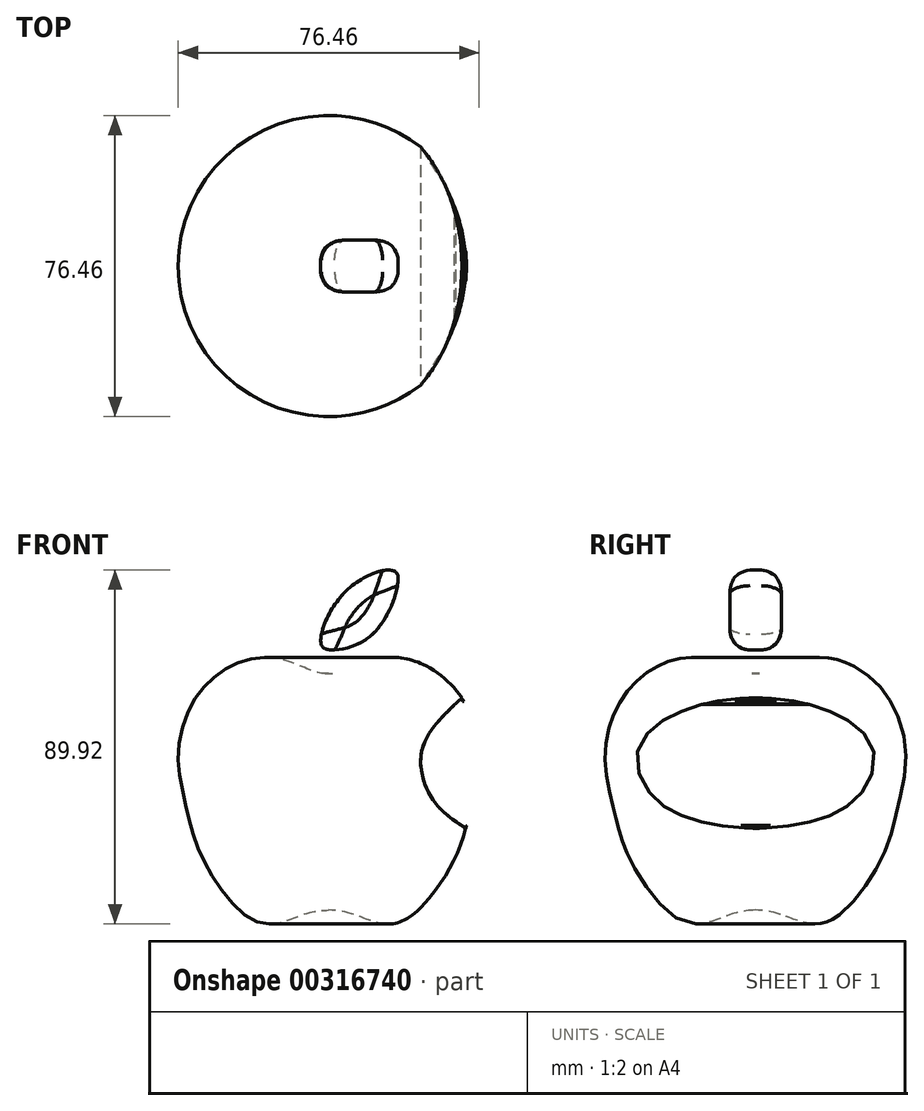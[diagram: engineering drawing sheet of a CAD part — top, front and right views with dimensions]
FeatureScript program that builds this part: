
annotation { "Feature Type Name" : "Feature", "Feature Type Description" : "" }
export const myFeature = defineFeature(function(context is Context, id is Id, definition is map)
    precondition{}
    {
        {
            var Q0;
            Q0=qCreatedBy(makeId("Front.planeOp"),FACE);
            var sketch = newSketch(context, id + "F0", { "sketchPlane" : qUnion([Q0])});
            skFitSpline(sketch, "E0", {"points": [v(0, 11.36) * mm, v(-2.96, 11.6) * mm, v(-11, 14.68) * mm, v(-20.48, 14.91) * mm, v(-28.76, 10.65) * mm, v(-35.15, 2.84) * mm, v(-38.23, -9.47) * mm, v(-36.57, -20.83) * mm, v(-33.73, -31.48) * mm, v(-28.29, -42.14) * mm, v(-19.06, -51.37) * mm, v(-11.95, -51.84) * mm, v(-5.09, -49.47) * mm, v(0, -48.76) * mm], "startDerivative": vector(-59.65, -3.1) * mm, "endDerivative": vector(84.75, 5.4) * mm});
            skLineSegment(sketch, "E1", {"start": v(0, 11.36) * mm, "end": v(0, -48.76) * mm});
            skLineSegment(sketch, "E2", {"start": v(0, 47.58) * mm, "end": v(0, -62.73) * mm, "construction": true});
            skSolve(sketch);
        }
        {
            var Q0;
            Q0=makeQuery(id+"F0.imprint","IMPRINT",FACE,{"disambiguationData":[TD([[makeQuery(id+"F0.imprint","IMPRINT",EDGE,{"derivedFrom":sQuery(id+"F0.wireOp",EDGE,"E0")}),1.0]])]});
            var Q1;
            Q1=sQuery(id+"F0.wireOp",EDGE,"E2");
            revolve(context, id + "F1", {"entities" : qUnion([Q0]), "axis" : qUnion([Q1]), "revolveType" : RevolveType.FULL});
        }
        {
            var Q0;
            Q0=qCreatedBy(makeId("Front.planeOp"),FACE);
            var sketch = newSketch(context, id + "F2", { "sketchPlane" : qUnion([Q0])});
            skFitSpline(sketch, "E3", {"points": [v(16.6, 37.42) * mm, v(4.82, 32.7) * mm, v(-2, 19.3) * mm, v(0, 17.41) * mm, v(10.7, 20.94) * mm, v(17.53, 33.89) * mm, v(16.6, 37.42) * mm]});
            skFitSpline(sketch, "E4", {"points": [v(34.54, 6.49) * mm, v(24.6, -3.3) * mm, v(23.65, -13.65) * mm, v(28.12, -23.06) * mm, v(35.18, -28.8) * mm, v(34.46, -29.02) * mm], "startDerivative": vector(-39.13, -36.51) * mm, "endDerivative": vector(-2.65, 8.88) * mm});
            skFitSpline(sketch, "E5", {"points": [v(34.52, -29.2) * mm, v(38.93, -14.77) * mm, v(34.52, 6.59) * mm, v(34.54, 6.49) * mm], "startDerivative": vector(14.06, 34.1) * mm, "endDerivative": vector(-15.1, 5.38) * mm});
            skLineSegment(sketch, "E6", {"start": v(34.54, 6.49) * mm, "end": v(34.52, -29.2) * mm, "construction": true});
            skLineSegment(sketch, "E7", {"start": v(34.73, 6.42) * mm, "end": v(34.71, -11.36) * mm});
            skPoint(sketch, "E7.endSnap0", {"position": v(34.53, -11.36) * mm});
            skSolve(sketch);
        }
        {
            var Q0;
            Q0=makeQuery(id+"F2.imprint","IMPRINT",FACE,{"disambiguationData":[TD([[makeQuery(id+"F2.imprint","IMPRINT",EDGE,{"derivedFrom":sQuery(id+"F2.wireOp",EDGE,"E3")}),1.0]])]});
            extrude(context, id + "F3", {"entities" : qUnion([Q0]), "endBound" : BoundingType.SYMMETRIC, "depth" : 13.13 * mm});
        }
        {
            var Q0;
            Q0=makeQuery(id+"F3.opExtrude","CAP_FACE",FACE,{"disambiguationData":[OSD([sQuery(id+"F2.wireOp",EDGE,"E3")])],"isStart":false});
            var Q1;
            Q1=makeQuery(id+"F3.opExtrude","CAP_EDGE",EDGE,{"disambiguationData":[OSD([sQuery(id+"F2.wireOp",EDGE,"E3")])],"isStart":true});
            fillet(context, id + "F4", {"entities" : qUnion([Q0, Q1]), "radius" : 5.08 * mm, "tangentPropagation" : true, "allowEdgeOverflow" : false});
        }
        {
            var Q0;
            Q0=qCreatedBy(makeId("Right.planeOp"),FACE);
            cPlane(context, id + "F5", {"entities" : qUnion([Q0]), "cplaneType" : CPlaneType.OFFSET, "offset" : 39.62 * mm, "width" : 152.4 * mm, "height" : 152.4 * mm});
        }
        {
            var Q0;
            Q0=qCreatedBy(makeId("Right.planeOp"),FACE);
            cPlane(context, id + "F6", {"entities" : qUnion([Q0]), "cplaneType" : CPlaneType.OFFSET, "offset" : 23.1 * mm, "width" : 152.4 * mm, "height" : 152.4 * mm});
        }
        {
            var Q0;
            Q0=qCreatedBy(makeId("Right.planeOp"),FACE);
            cPlane(context, id + "F7", {"entities" : qUnion([Q0]), "cplaneType" : CPlaneType.OFFSET, "offset" : 30.48 * mm, "width" : 152.4 * mm, "height" : 152.4 * mm});
        }
        {
            var Q0;
            Q0=qCreatedBy(makeId("Front.planeOp"),FACE);
            var sketch = newSketch(context, id + "F8", { "sketchPlane" : qUnion([Q0])});
            skFitSpline(sketch, "E8", {"points": [v(33.94, 5.23) * mm, v(25.86, -3.37) * mm, v(23.37, -11.03) * mm, v(26.67, -21.01) * mm, v(34.83, -28) * mm], "startDerivative": vector(-34.13, -31.9) * mm, "endDerivative": vector(35.43, -23.64) * mm});
            skLineSegment(sketch, "E9", {"start": v(34.83, -28) * mm, "end": v(33.94, 5.23) * mm});
            skSolve(sketch);
        }
        {
            var Q0;
            Q0=makeQuery(id+"F8.imprint","IMPRINT",FACE,{"disambiguationData":[TD([[makeQuery(id+"F8.imprint","IMPRINT",EDGE,{"derivedFrom":sQuery(id+"F8.wireOp",EDGE,"E8")}),1.0]])]});
            extrude(context, id + "F9", {"entities" : qUnion([Q0]), "operationType" : NewBodyOperationType.REMOVE, "endBound" : BoundingType.SYMMETRIC, "depth" : 101.6 * mm});
        }
        {
            var Q0;
            Q0=qCreatedBy(makeId("Front.planeOp"),FACE);
            var sketch = newSketch(context, id + "F10", { "sketchPlane" : qUnion([Q0])});
            skFitSpline(sketch, "E10", {"points": [v(33.77, 4.24) * mm, v(50.71, -10.82) * mm, v(35.42, -27.53) * mm, v(30.7, -4.94) * mm, v(33.77, 4.24) * mm]});
            skSolve(sketch);
        }
        {
            var Q0;
            Q0=makeQuery(id+"F10.imprint","IMPRINT",FACE,{"disambiguationData":[TD([[makeQuery(id+"F10.imprint","IMPRINT",EDGE,{"derivedFrom":sQuery(id+"F10.wireOp",EDGE,"E10")}),-1.0]])]});
            extrude(context, id + "F11", {"entities" : qUnion([Q0]), "operationType" : NewBodyOperationType.REMOVE, "endBound" : BoundingType.SYMMETRIC, "oppositeDirection" : true, "depth" : 34.04 * mm});
        }
    });
